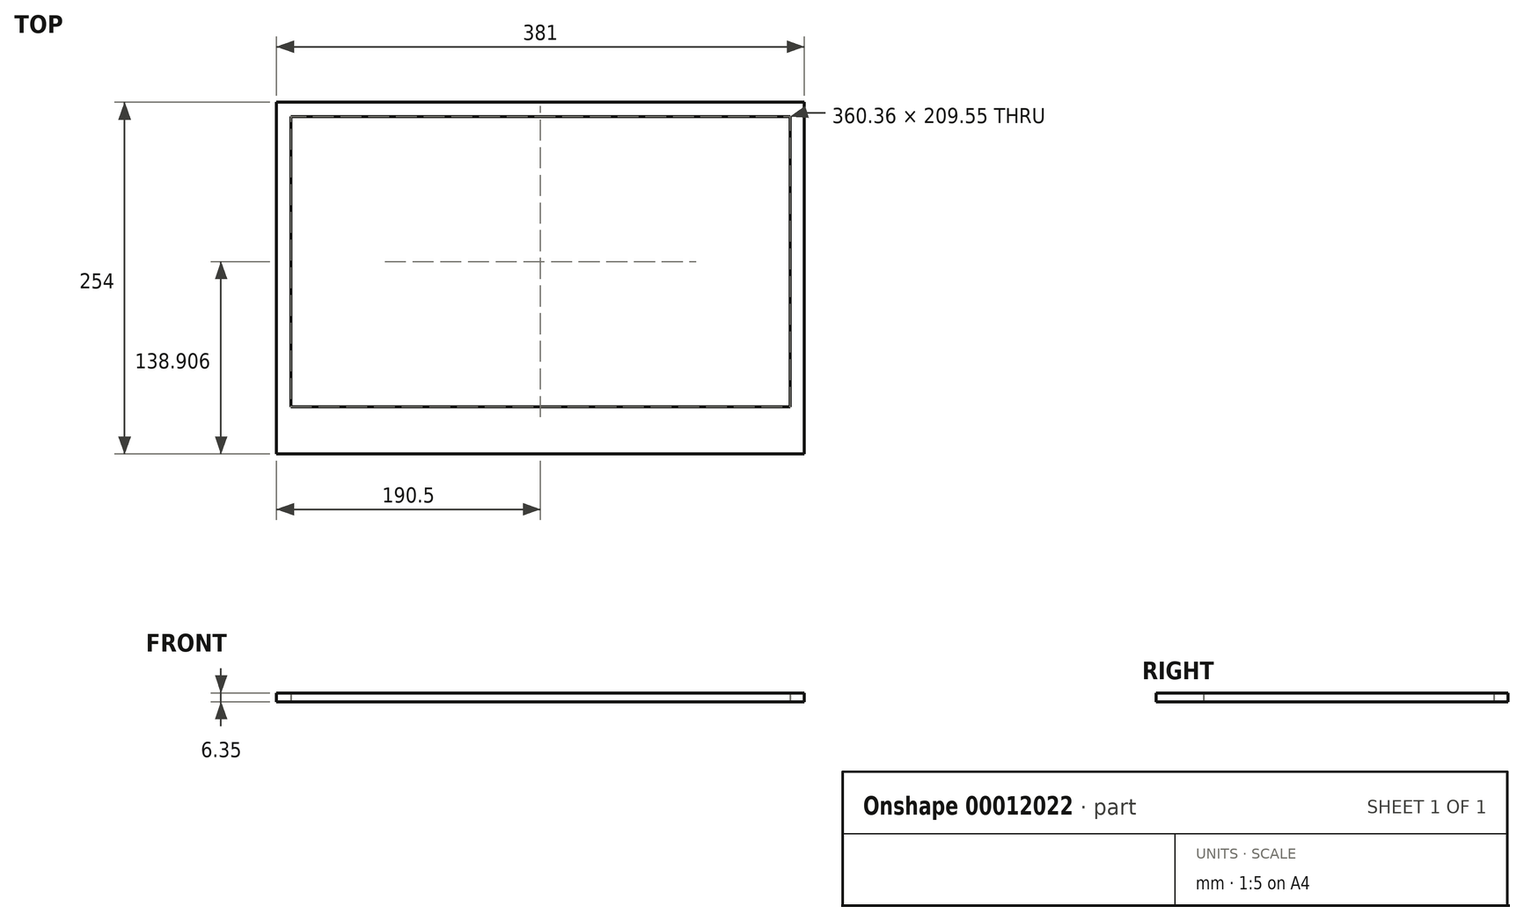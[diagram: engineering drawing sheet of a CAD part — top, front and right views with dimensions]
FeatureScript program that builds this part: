
annotation { "Feature Type Name" : "Feature", "Feature Type Description" : "" }
export const myFeature = defineFeature(function(context is Context, id is Id, definition is map)
    precondition{}
    {
        {
            var Q0;
            Q0=qCreatedBy(makeId("Top.planeOp"),FACE);
            var sketch = newSketch(context, id + "F0", { "sketchPlane" : qUnion([Q0])});
            skLineSegment(sketch, "E0.rect.bottom", {"start": v(190.5, 127) * mm, "end": v(-190.5, 127) * mm});
            skLineSegment(sketch, "E0.rect.top", {"start": v(190.5, -127) * mm, "end": v(-190.5, -127) * mm});
            skLineSegment(sketch, "E0.rect.left", {"start": v(190.5, 127) * mm, "end": v(190.5, -127) * mm});
            skLineSegment(sketch, "E0.rect.right", {"start": v(-190.5, 127) * mm, "end": v(-190.5, -127) * mm});
            skLineSegment(sketch, "E1.rect.bottom", {"start": v(180.18, 116.68) * mm, "end": v(-180.18, 116.68) * mm});
            skLineSegment(sketch, "E1.rect.top", {"start": v(180.18, -92.87) * mm, "end": v(-180.18, -92.87) * mm});
            skLineSegment(sketch, "E1.rect.left", {"start": v(180.18, 116.68) * mm, "end": v(180.18, -92.87) * mm});
            skLineSegment(sketch, "E1.rect.right", {"start": v(-180.18, 116.68) * mm, "end": v(-180.18, -92.87) * mm});
            skSolve(sketch);
        }
        {
            var Q0;
            Q0=makeQuery(id+"F0.imprint","IMPRINT",FACE,{"disambiguationData":[TD([[makeQuery(id+"F0.imprint","IMPRINT",EDGE,{"derivedFrom":sQuery(id+"F0.wireOp",EDGE,"E0.rect.bottom")}),1.0]])]});
            extrude(context, id + "F1", {"entities" : qUnion([Q0]), "depth" : 6.35 * mm});
        }
    });
